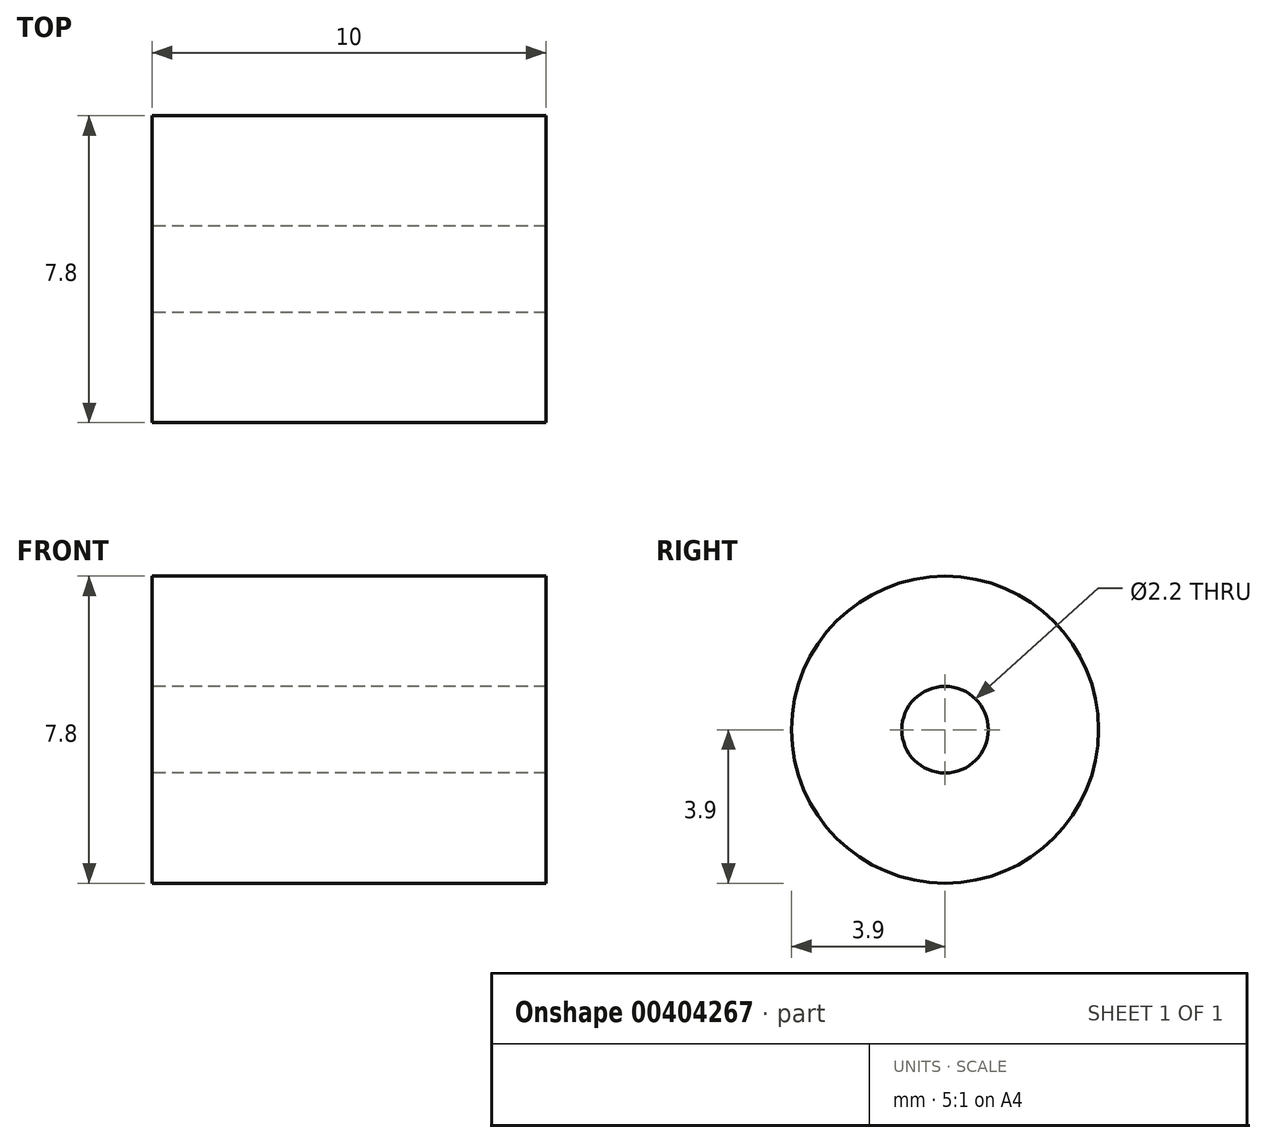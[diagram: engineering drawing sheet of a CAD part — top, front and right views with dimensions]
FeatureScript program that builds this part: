
annotation { "Feature Type Name" : "Feature", "Feature Type Description" : "" }
export const myFeature = defineFeature(function(context is Context, id is Id, definition is map)
    precondition{}
    {
        {
            var Q0;
            Q0=qCreatedBy(makeId("Right.planeOp"),FACE);
            var sketch = newSketch(context, id + "F0", { "sketchPlane" : qUnion([Q0])});
            skCircle(sketch, "E0", {"center": v(0, 0) * mm, "radius": 3.9 * mm});
            skCircle(sketch, "E1", {"center": v(0, 0) * mm, "radius": 1.1 * mm});
            skSolve(sketch);
        }
        {
            var Q0;
            Q0=makeQuery(id+"F0.imprint","IMPRINT",FACE,{"disambiguationData":[TD([[makeQuery(id+"F0.imprint","IMPRINT",EDGE,{"derivedFrom":sQuery(id+"F0.wireOp",EDGE,"E0")}),1.0]])]});
            extrude(context, id + "F1", {"entities" : qUnion([Q0]), "depth" : 10 * mm});
        }
    });
